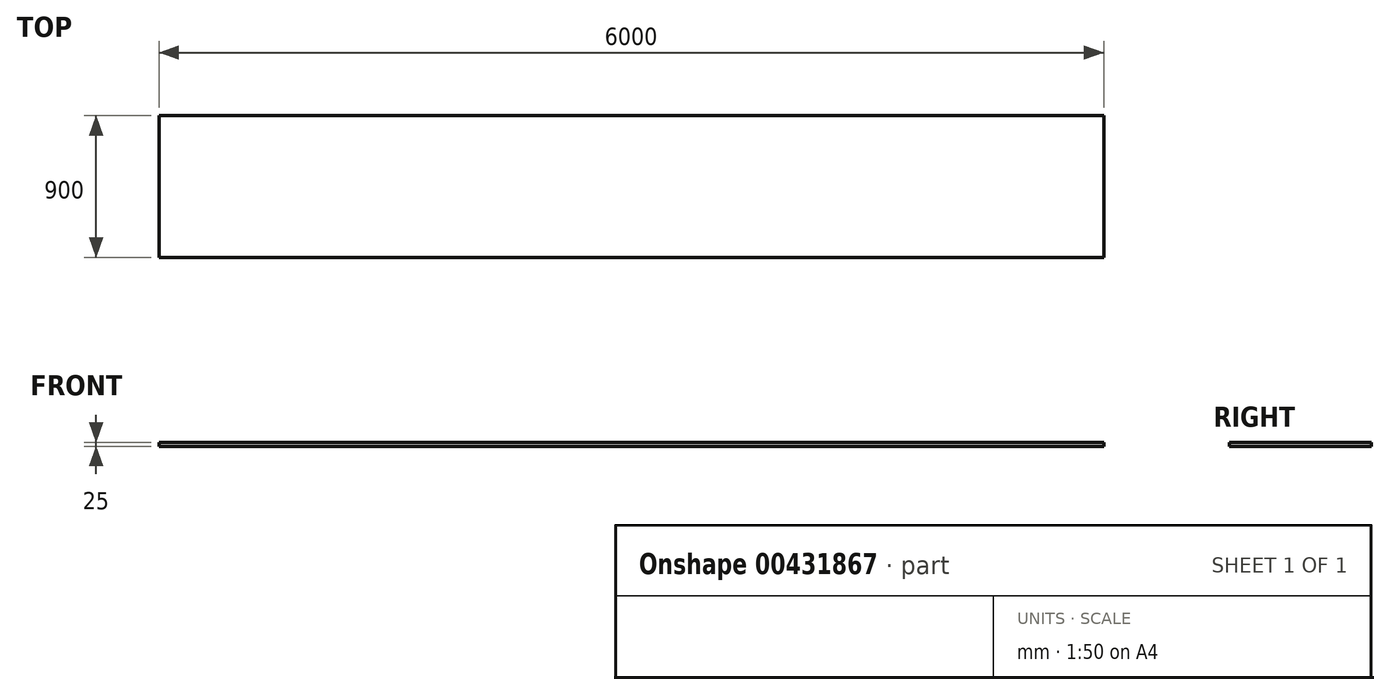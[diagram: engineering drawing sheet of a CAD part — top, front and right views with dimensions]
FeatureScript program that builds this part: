
annotation { "Feature Type Name" : "Feature", "Feature Type Description" : "" }
export const myFeature = defineFeature(function(context is Context, id is Id, definition is map)
    precondition{}
    {
        {
            var Q0;
            Q0=qCreatedBy(makeId("Top.planeOp"),FACE);
            var sketch = newSketch(context, id + "F0", { "sketchPlane" : qUnion([Q0])});
            skLineSegment(sketch, "E0.bottom", {"start": v(-89.73, -41.26) * mm, "end": v(5910.27, -41.26) * mm});
            skLineSegment(sketch, "E0.top", {"start": v(-89.73, 858.74) * mm, "end": v(5910.27, 858.74) * mm});
            skLineSegment(sketch, "E0.left", {"start": v(-89.73, -41.26) * mm, "end": v(-89.73, 858.74) * mm});
            skLineSegment(sketch, "E0.right", {"start": v(5910.27, -41.26) * mm, "end": v(5910.27, 858.74) * mm});
            skSolve(sketch);
        }
        {
            var Q0;
            Q0=makeQuery(id+"F0.imprint","IMPRINT",FACE,{"disambiguationData":[TD([[makeQuery(id+"F0.imprint","IMPRINT",EDGE,{"derivedFrom":sQuery(id+"F0.wireOp",EDGE,"E0.bottom")}),1.0]])]});
            extrude(context, id + "F1", {"entities" : qUnion([Q0]), "depth" : 25 * mm, "offsetDistance" : 25 * mm});
        }
    });
